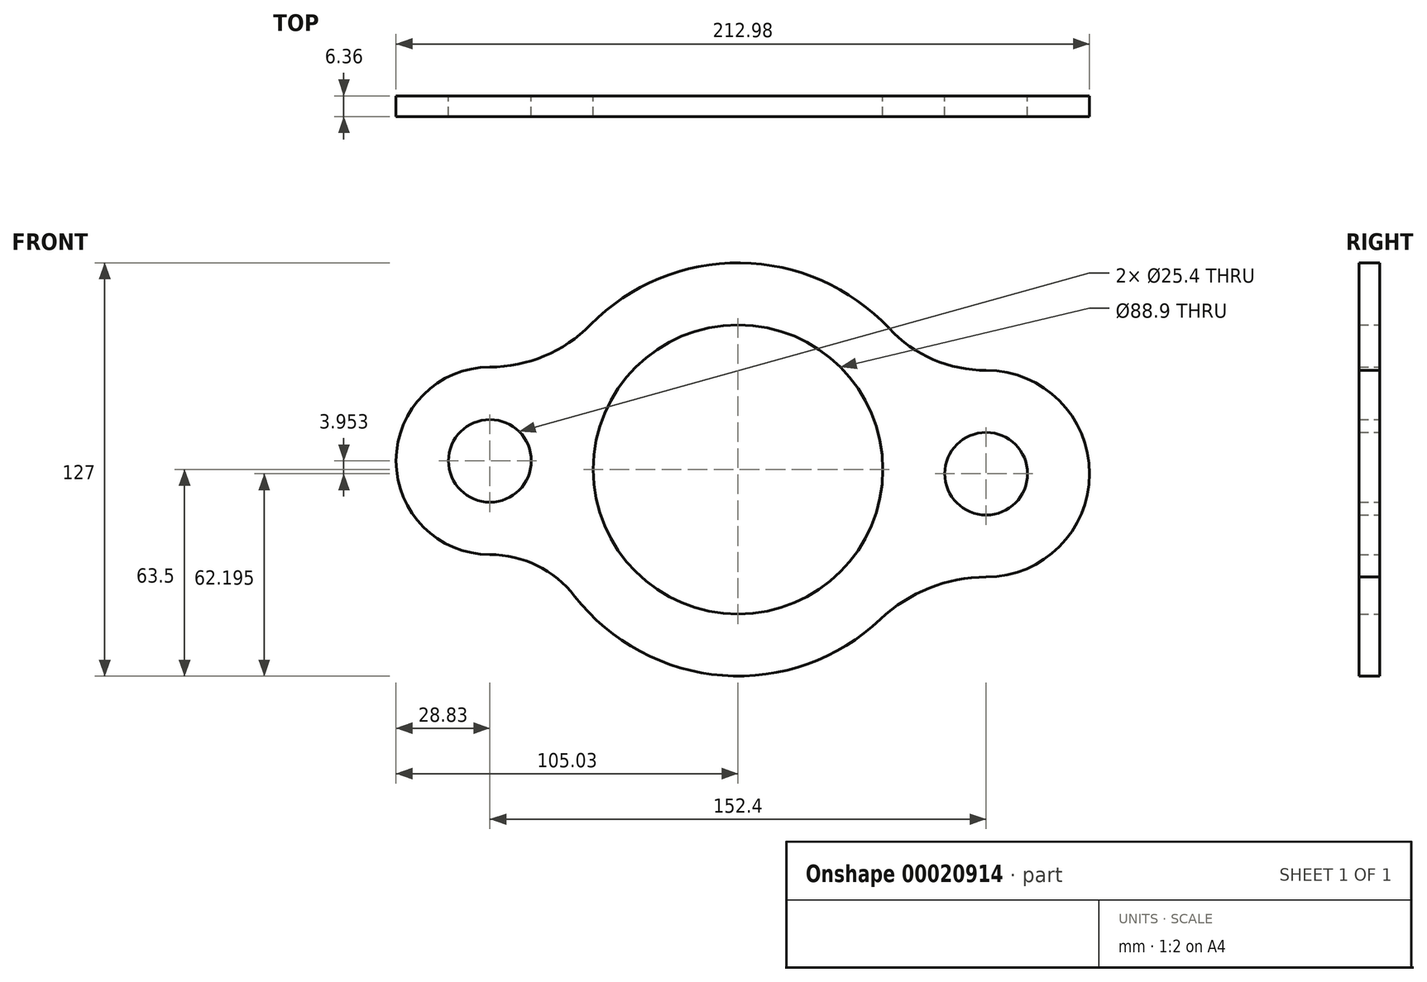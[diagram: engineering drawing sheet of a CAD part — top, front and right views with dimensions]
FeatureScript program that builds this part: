
annotation { "Feature Type Name" : "Feature", "Feature Type Description" : "" }
export const myFeature = defineFeature(function(context is Context, id is Id, definition is map)
    precondition{}
    {
        {
            var Q0;
            Q0=qCreatedBy(makeId("Front.planeOp"),FACE);
            var sketch = newSketch(context, id + "F0", { "sketchPlane" : qUnion([Q0])});
            skCircle(sketch, "E0", {"center": v(0, 0) * mm, "radius": 44.45 * mm});
            skArc(sketch, "E1", {"start": v(-50.16, -38.94) * mm, "mid": v(-4.77, -63.32) * mm, "end": v(43.76, -46.02) * mm});
            skCircle(sketch, "E2", {"center": v(-76.2, 2.65) * mm, "radius": 12.7 * mm});
            skCircle(sketch, "E3", {"center": v(76.2, -1.3) * mm, "radius": 12.7 * mm});
            skArc(sketch, "E4", {"start": v(-76.2, 31.48) * mm, "mid": v(-105.03, 2.65) * mm, "end": v(-76.2, -26.19) * mm});
            skArc(sketch, "E5", {"start": v(76.2, -33.06) * mm, "mid": v(107.95, -1.3) * mm, "end": v(76.2, 30.44) * mm});
            skArc(sketch, "E6", {"start": v(-50.16, -38.94) * mm, "mid": v(-61.7, -29.55) * mm, "end": v(-76.2, -26.19) * mm});
            skArc(sketch, "E7", {"start": v(76.2, -33.06) * mm, "mid": v(58.73, -36.42) * mm, "end": v(43.76, -46.02) * mm});
            skArc(sketch, "E8", {"start": v(-76.2, 31.48) * mm, "mid": v(-59.47, 34.85) * mm, "end": v(-45.36, 44.44) * mm});
            skArc(sketch, "E9.trimOffspring", {"start": v(46.37, 43.39) * mm, "mid": v(0.73, 63.5) * mm, "end": v(-45.36, 44.44) * mm});
            skArc(sketch, "E10", {"start": v(46.37, 43.39) * mm, "mid": v(59.94, 33.82) * mm, "end": v(76.2, 30.44) * mm});
            skSolve(sketch);
        }
        {
            var Q0;
            Q0=makeQuery(id+"F0.imprint","IMPRINT",FACE,{"disambiguationData":[TD([[makeQuery(id+"F0.imprint","IMPRINT",EDGE,{"derivedFrom":sQuery(id+"F0.wireOp",EDGE,"E0")}),-1.0]])]});
            extrude(context, id + "F1", {"entities" : qUnion([Q0]), "depth" : 6.35 * mm, "symmetric" : true});
        }
    });
